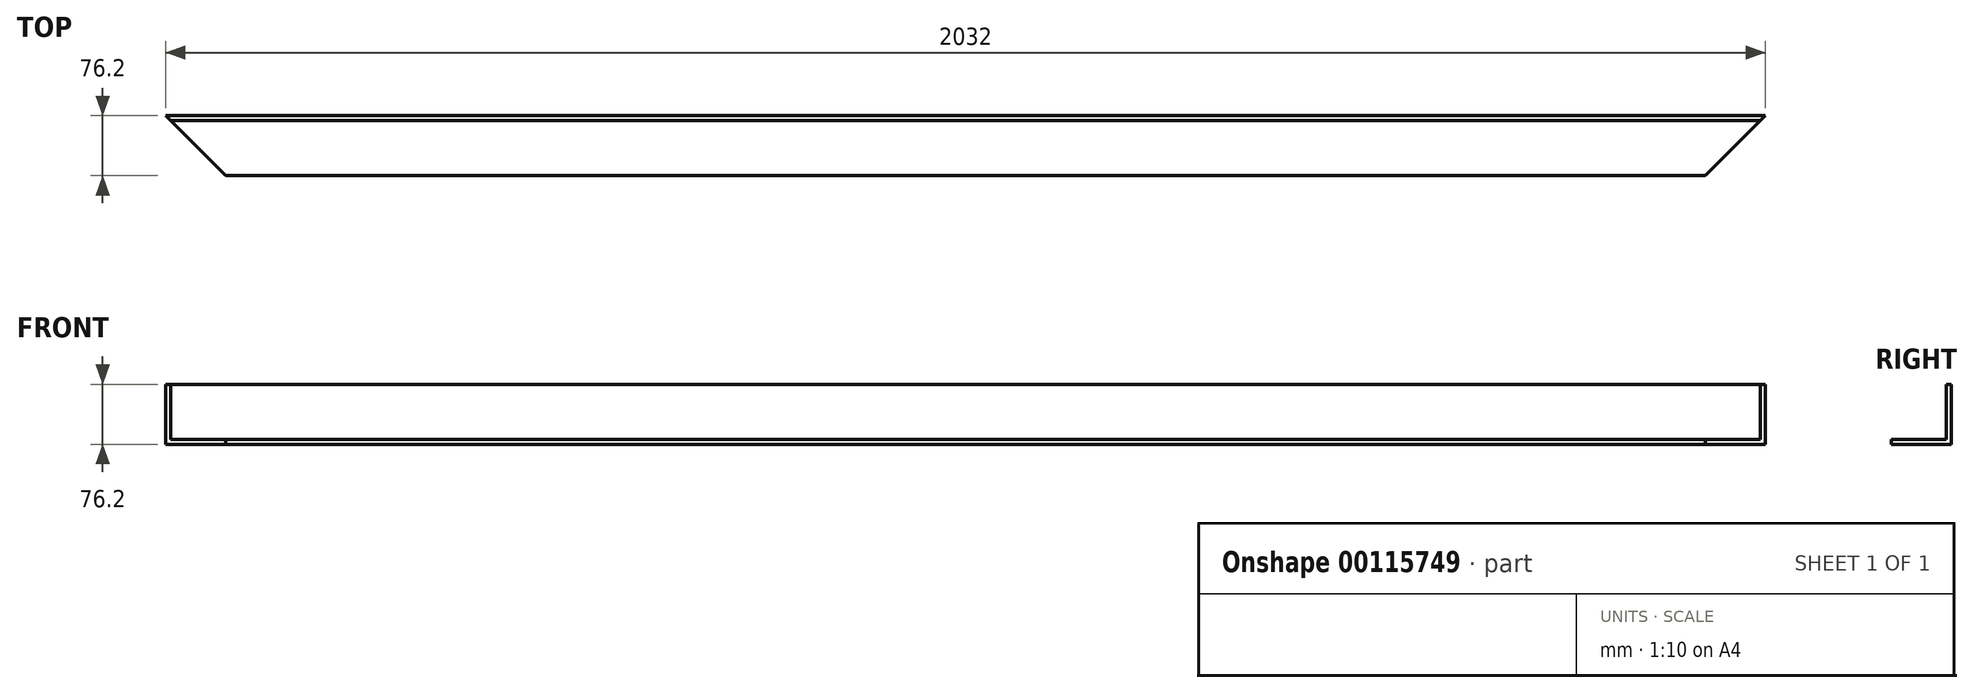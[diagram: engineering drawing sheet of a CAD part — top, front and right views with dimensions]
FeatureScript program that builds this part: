
annotation { "Feature Type Name" : "Feature", "Feature Type Description" : "" }
export const myFeature = defineFeature(function(context is Context, id is Id, definition is map)
    precondition{}
    {
        {
            var Q0;
            Q0=qCreatedBy(makeId("Top.planeOp"),FACE);
            var sketch = newSketch(context, id + "F0", { "sketchPlane" : qUnion([Q0])});
            skLineSegment(sketch, "E0", {"start": v(0, 0) * mm, "end": v(-2032, 0) * mm});
            skLineSegment(sketch, "E1.0", {"start": v(0, 76.2) * mm, "end": v(-2032, 76.2) * mm});
            skLineSegment(sketch, "E2", {"start": v(-2032, 76.2) * mm, "end": v(-2032, 0) * mm});
            skLineSegment(sketch, "E3", {"start": v(0, 76.2) * mm, "end": v(0, 0) * mm});
            skSolve(sketch);
        }
        {
            var Q0;
            Q0 = qSketchRegion(id + "F0", true);
            extrude(context, id + "F1", {"entities" : qUnion([Q0]), "oppositeDirection" : true, "depth" : 76.2 * mm});
        }
        {
            var Q0;
            Q0=makeQuery(id+"F1.opExtrude","CAP_FACE",FACE,{"disambiguationData":[OSD([sQuery(id+"F0.wireOp",EDGE,"E0"),sQuery(id+"F0.wireOp",EDGE,"E1.0"),sQuery(id+"F0.wireOp",EDGE,"E2"),sQuery(id+"F0.wireOp",EDGE,"E3")])],"isStart":true});
            var sketch = newSketch(context, id + "F2", { "sketchPlane" : qUnion([Q0])});
            skLineSegment(sketch, "E4.2", {"start": v(0, 0) * mm, "end": v(-2032, 0) * mm});
            skLineSegment(sketch, "E5.0", {"start": v(0, 69.85) * mm, "end": v(-2032, 69.85) * mm});
            skLineSegment(sketch, "E6", {"start": v(-2032, 69.85) * mm, "end": v(-2032, 0) * mm});
            skLineSegment(sketch, "E7", {"start": v(0, 69.85) * mm, "end": v(0, 0) * mm});
            skSolve(sketch);
        }
        {
            var Q0;
            Q0 = qSketchRegion(id + "F2", true);
            extrude(context, id + "F3", {"entities" : qUnion([Q0]), "operationType" : NewBodyOperationType.REMOVE, "oppositeDirection" : true, "depth" : 69.85 * mm});
        }
        {
            var Q0;
            Q0=makeQuery(id+"F1.opExtrude","CAP_FACE",FACE,{"disambiguationData":[OSD([sQuery(id+"F0.wireOp",EDGE,"E0"),sQuery(id+"F0.wireOp",EDGE,"E1.0"),sQuery(id+"F0.wireOp",EDGE,"E2"),sQuery(id+"F0.wireOp",EDGE,"E3")])],"isStart":true});
            var sketch = newSketch(context, id + "F4", { "sketchPlane" : qUnion([Q0])});
            skLineSegment(sketch, "E8", {"start": v(-2032, 76.2) * mm, "end": v(-1955.8, 0) * mm});
            skLineSegment(sketch, "E9", {"start": v(-76.2, 0) * mm, "end": v(0, 76.2) * mm});
            skLineSegment(sketch, "E10", {"start": v(-76.2, 0) * mm, "end": v(0, 0) * mm});
            skLineSegment(sketch, "E11", {"start": v(0, 0) * mm, "end": v(0, 76.2) * mm});
            skLineSegment(sketch, "E12", {"start": v(-1955.8, 0) * mm, "end": v(-2032, 0) * mm});
            skLineSegment(sketch, "E13", {"start": v(-2032, 0) * mm, "end": v(-2032, 76.2) * mm});
            skSolve(sketch);
        }
        {
            var Q0;
            Q0 = qSketchRegion(id + "F4", true);
            extrude(context, id + "F5", {"entities" : qUnion([Q0]), "operationType" : NewBodyOperationType.REMOVE, "oppositeDirection" : true, "depth" : 76.2 * mm});
        }
    });
